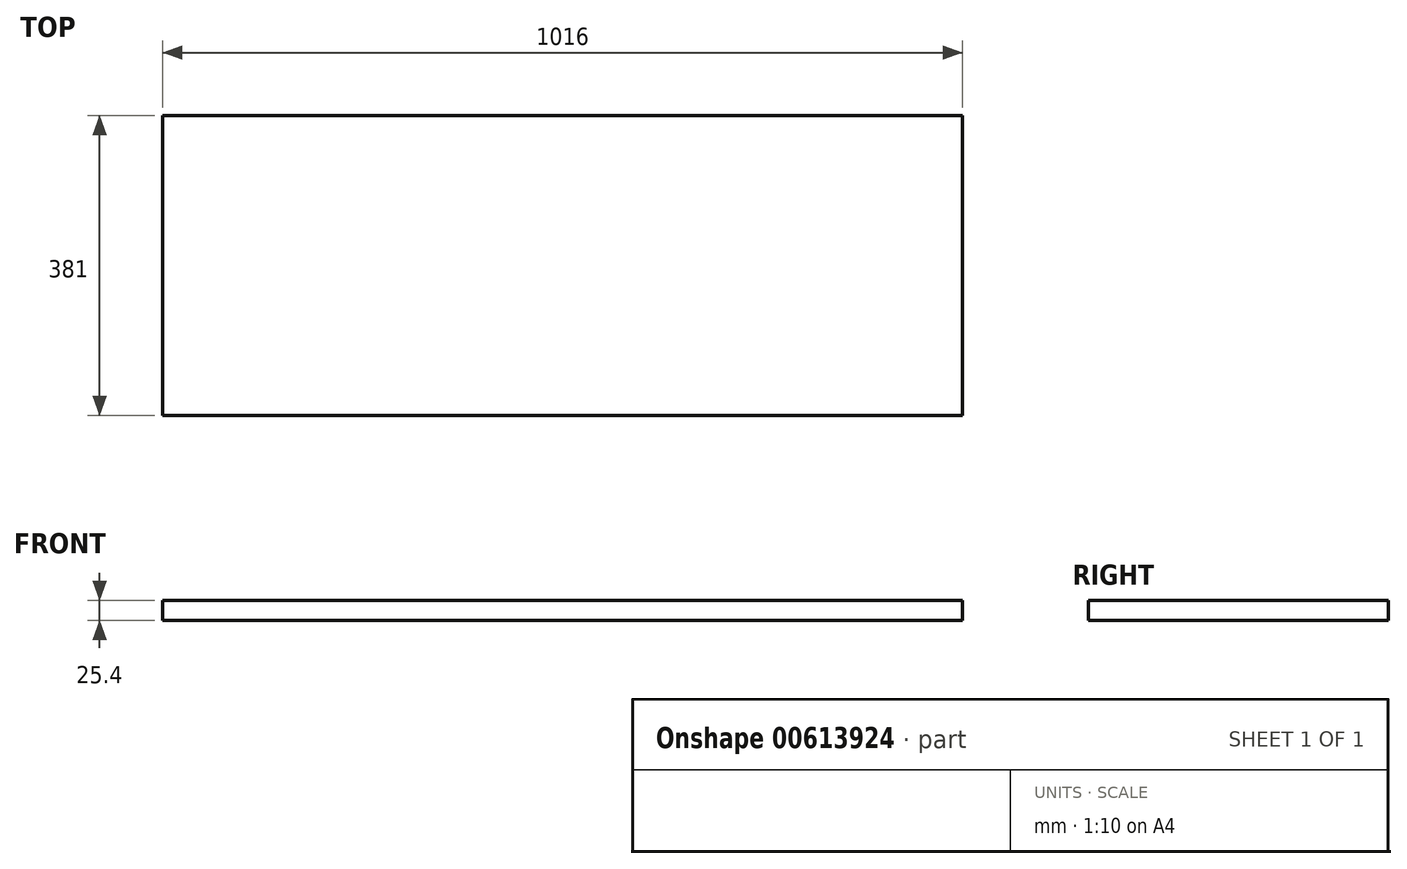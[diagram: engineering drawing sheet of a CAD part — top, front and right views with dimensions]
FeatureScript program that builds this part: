
annotation { "Feature Type Name" : "Feature", "Feature Type Description" : "" }
export const myFeature = defineFeature(function(context is Context, id is Id, definition is map)
    precondition{}
    {
        {
            var Q0;
            Q0=qCreatedBy(makeId("Top.planeOp"),FACE);
            var sketch = newSketch(context, id + "F0", { "sketchPlane" : qUnion([Q0])});
            skLineSegment(sketch, "E0", {"start": v(-452.9, 192.8) * mm, "end": v(563.1, 192.8) * mm});
            skLineSegment(sketch, "E1", {"start": v(563.1, 192.8) * mm, "end": v(563.1, -188.2) * mm});
            skLineSegment(sketch, "E2", {"start": v(563.1, -188.2) * mm, "end": v(-452.9, -188.2) * mm});
            skLineSegment(sketch, "E3", {"start": v(-452.9, -188.2) * mm, "end": v(-452.9, 192.8) * mm});
            skSolve(sketch);
        }
        {
            var Q0;
            Q0=makeQuery(id+"F0.imprint","IMPRINT",FACE,{"disambiguationData":[TD([[makeQuery(id+"F0.imprint","IMPRINT",EDGE,{"derivedFrom":sQuery(id+"F0.wireOp",EDGE,"E0")}),-1.0]])]});
            extrude(context, id + "F1", {"entities" : qUnion([Q0]), "depth" : 25.4 * mm, "offsetDistance" : 25.4 * mm});
        }
    });
